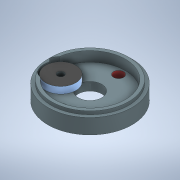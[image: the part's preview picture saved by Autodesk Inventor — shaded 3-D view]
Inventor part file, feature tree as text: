
AUTODESK INVENTOR PART (.ipt)
format: ipt  version: 2020 (Build 240168000, 168)  size: 195,584 bytes
history: native  units: mm
features: extrude x9, sketch x9, other x1
ambient origin geometry x8: Origin, YZ Plane, XZ Plane, XY Plane, X Axis, Y Axis, Z Axis, Center Point
bodies: Body1 (feature_tree)
feature tree (19):
  other  "Bryła1"
  extrude  "Wyciągnięcie proste1"  Depth=25.0mm
  extrude  "Wyciągnięcie proste2"  Depth=2.5mm TaperAngle=0.0deg
  extrude  "Wyciągnięcie proste3"  Depth=7.0mm
  extrude  "Wyciągnięcie proste4"  Depth=2.5mm TaperAngle=0.0deg
  extrude  "Wyciągnięcie proste6"  Depth=3.0mm
  extrude  "Wyciągnięcie proste7"  Depth=3.0mm
  extrude  "Wyciągnięcie proste5"  Depth=17.0mm
  extrude  "Wyciągnięcie proste8"  Depth=8.5mm
  extrude  "Wyciągnięcie proste9"  Depth=2.5mm TaperAngle=0.0deg
  sketch  "Szkic1"
  sketch  "Szkic2"
  sketch  "Szkic3"
  sketch  "Szkic4"
  sketch  "Szkic5"
  sketch  "Szkic6"
  sketch  "Szkic7"
  sketch  "Szkic8"
  sketch  "Szkic9"
